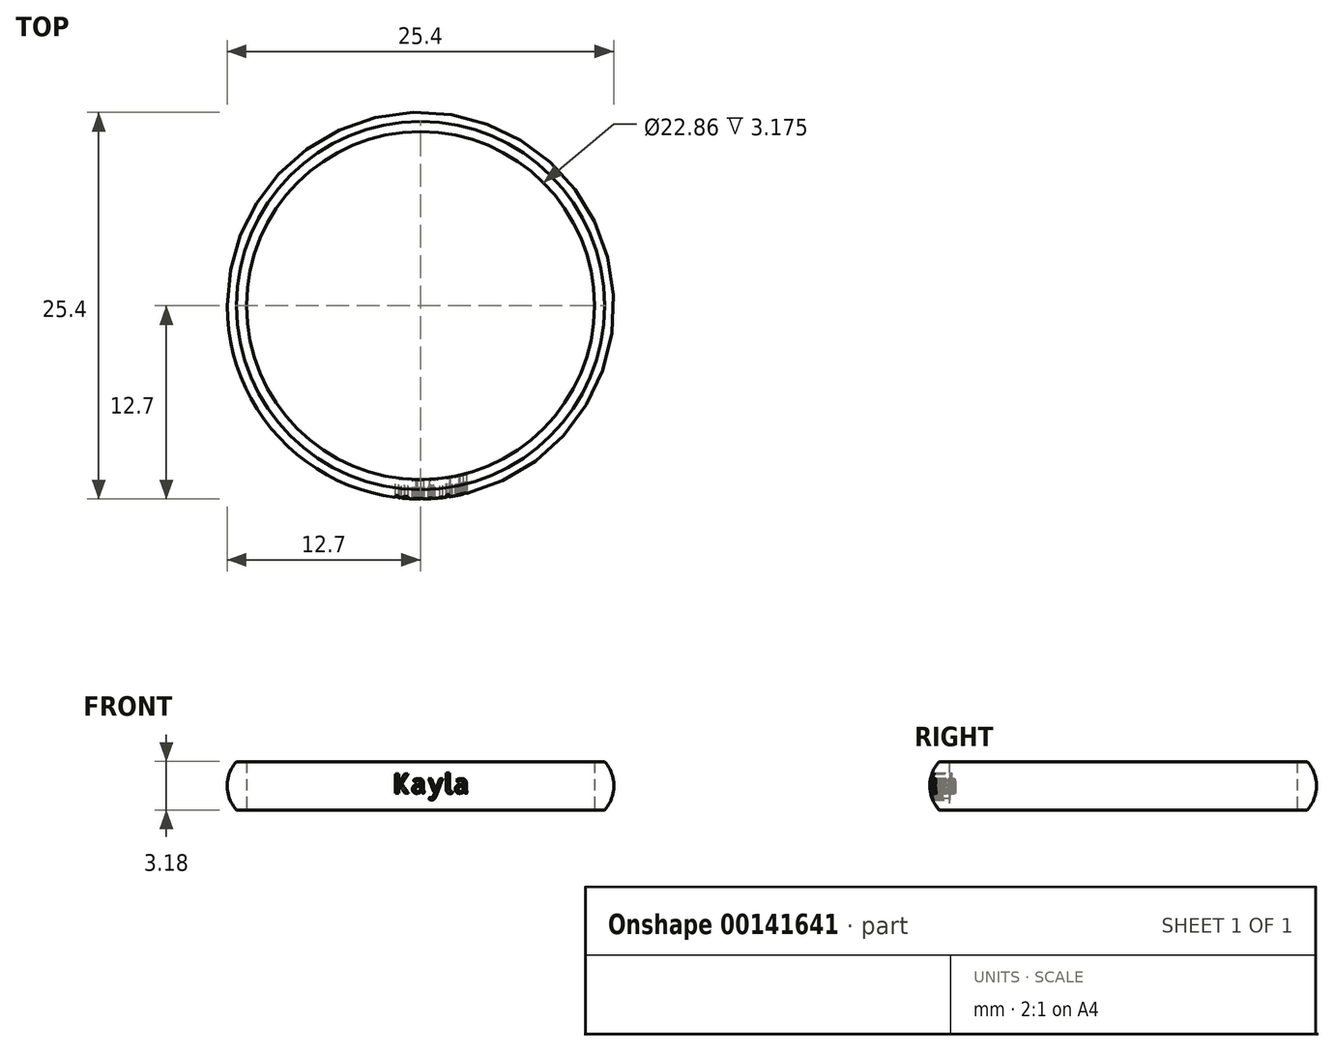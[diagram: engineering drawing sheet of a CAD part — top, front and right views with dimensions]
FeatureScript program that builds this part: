
annotation { "Feature Type Name" : "Feature", "Feature Type Description" : "" }
export const myFeature = defineFeature(function(context is Context, id is Id, definition is map)
    precondition{}
    {
        {
            var Q0;
            Q0=qCreatedBy(makeId("Front.planeOp"),FACE);
            var sketch = newSketch(context, id + "F0", { "sketchPlane" : qUnion([Q0])});
            skLineSegment(sketch, "E0.bottom", {"start": v(11.43, 1.59) * mm, "end": v(12.7, 1.59) * mm});
            skLineSegment(sketch, "E0.top", {"start": v(11.43, -1.59) * mm, "end": v(12.7, -1.59) * mm});
            skLineSegment(sketch, "E0.left", {"start": v(11.43, 1.59) * mm, "end": v(11.43, -1.59) * mm});
            skLineSegment(sketch, "E0.right", {"start": v(12.7, 1.59) * mm, "end": v(12.7, -1.59) * mm});
            skLineSegment(sketch, "E1", {"start": v(0, 0) * mm, "end": v(0, 3.1) * mm, "construction": true});
            skLineSegment(sketch, "E2", {"start": v(0, 0) * mm, "end": v(4.57, 0) * mm, "construction": true});
            skSolve(sketch);
        }
        {
            var Q0;
            Q0 = qSketchRegion(id + "F0", true);
            var Q1;
            Q1=sQuery(id+"F0.wireOp",EDGE,"E1");
            revolve(context, id + "F1", {"entities" : qUnion([Q0]), "axis" : qUnion([Q1]), "revolveType" : RevolveType.FULL});
        }
        {
            var Q0;
            Q0=qCreatedBy(makeId("Front.planeOp"),FACE);
            var sketch = newSketch(context, id + "F2", { "sketchPlane" : qUnion([Q0])});
            skArc(sketch, "E3", {"start": v(10.25, -2.38) * mm, "mid": v(12.7, -0.02) * mm, "end": v(10.3, 2.38) * mm});
            skLineSegment(sketch, "E4", {"start": v(10.3, 2.38) * mm, "end": v(10.3, 3.83) * mm});
            skLineSegment(sketch, "E5", {"start": v(10.3, 3.83) * mm, "end": v(15.3, 3.83) * mm});
            skLineSegment(sketch, "E6", {"start": v(15.3, 3.83) * mm, "end": v(15.3, -3.28) * mm});
            skLineSegment(sketch, "E7", {"start": v(15.3, -3.28) * mm, "end": v(10.25, -3.28) * mm});
            skLineSegment(sketch, "E8", {"start": v(10.25, -3.28) * mm, "end": v(10.25, -2.38) * mm});
            skSolve(sketch);
        }
        {
            var Q0;
            Q0 = qSketchRegion(id + "F2", true);
            var Q1;
            Q1=sQuery(id+"F0.wireOp",EDGE,"E1");
            revolve(context, id + "F3", {"operationType" : NewBodyOperationType.REMOVE, "entities" : qUnion([Q0]), "axis" : qUnion([Q1]), "revolveType" : RevolveType.FULL, "oppositeDirection" : true});
        }
        {
            var Q0;
            Q0=qCreatedBy(makeId("Front.planeOp"),FACE);
            var sketch = newSketch(context, id + "F4", { "sketchPlane" : qUnion([Q0])});
            skText(sketch, "E9", { "text": "Kayla", "fontName": "AllertaStencil-Regular.ttf"});
            const initialGuessF4  = {"E9": [-0.0018, -0.0005, 1, 0, 0.00127]};
            skSetInitialGuess(sketch, initialGuessF4);
            skSolve(sketch);
        }
        {
            var Q0;
            Q0 = qSketchRegion(id + "F4", true);
            var Q1;
            Q1=makeQuery(id+"F1.opRevolve","SWEPT_FACE",FACE,{"disambiguationData":[OSD([sQuery(id+"F0.wireOp",EDGE,"E0.left")])]});
            extrude(context, id + "F5", {"entities" : qUnion([Q0]), "operationType" : NewBodyOperationType.REMOVE, "endBoundEntityFace" : qUnion([Q1]), "depth" : 28.65 * mm});
        }
    });
